# Revit family: Faucet-Centerset-American_Standard-Monterrey-7500.180.002
name_source: partatom
category: Plumbing Fixtures
revit_build: Autodesk Revit 2018 (Build: 20170223_1515(x64)
units: mm (PartAtom-declared; Revit-internal decimal feet)

## family parameters
Always vertical = No
Cut with Voids When Loaded = No
OmniClass Number = 23.45.55.17
OmniClass Title = Mixing Faucets
Part Type = Normal
Room Calculation Point = No
Round Connector Dimension = Use Diameter
Shared = Yes
Work Plane-Based = Yes

## types (1)
- 7500.180.002
    -L10 1.0 gpm (3.8 Lpm) PCA Non-Aerated Laminar Flow Outlet = No
    ADA Compliant = Yes
    Assembly Code = D2020300
    CW Connection = Yes
    CWFU = 1.5
    Cold Water Connection Diameter = 1/2"
    Default Elevation = 0"
    Description = Monterrey 4 Inch Centerset Gooseneck Faucet, 1.5 gpm Laminar Flow in Spout Base, 5 Inch Spout Reach
    Finish = Cast Brass-American Standard-002-Polished Chrome
    Flow Rate = 1.5 gpm (5.7lpm)
    HW Connection = Yes
    HWFU = 1.5
    Height = 10 3/4"
    Hot Water Connection Diameter = 1/2"
    IAPMO Compliance = Product meet or exceeds ANSI 117.1 , ASME A112.18.1, CSA B 125, NSF 372
    Installation Type = Deck Mounted
    Length = 6 3/8"
    Manufacturer = American Standard
    Material = Cast Brass-American Standard-002-Polished Chrome
    Model = 7500.180.002
    Price = Prices may vary. Please consult Manufacturer Representative for most up-to-date price list.
    Product Documentation Link = https://americanstandard.box.com
    Product Page URL = https://www.americanstandard-us.com
    Revised Date = 05/03/2021
    Spout Reach = 5"
    URL = http://www.americanstandard-us.com
    Vent Connection = No
    WFU = 2
    Warranty Information = Commercial 2-yr Limited Warranty
    Waste Connection = No
    Width = 11 3/4"

## geometry (parser evidence)
native form markers: Sweep x2
no freeform markers — native parametric forms only
